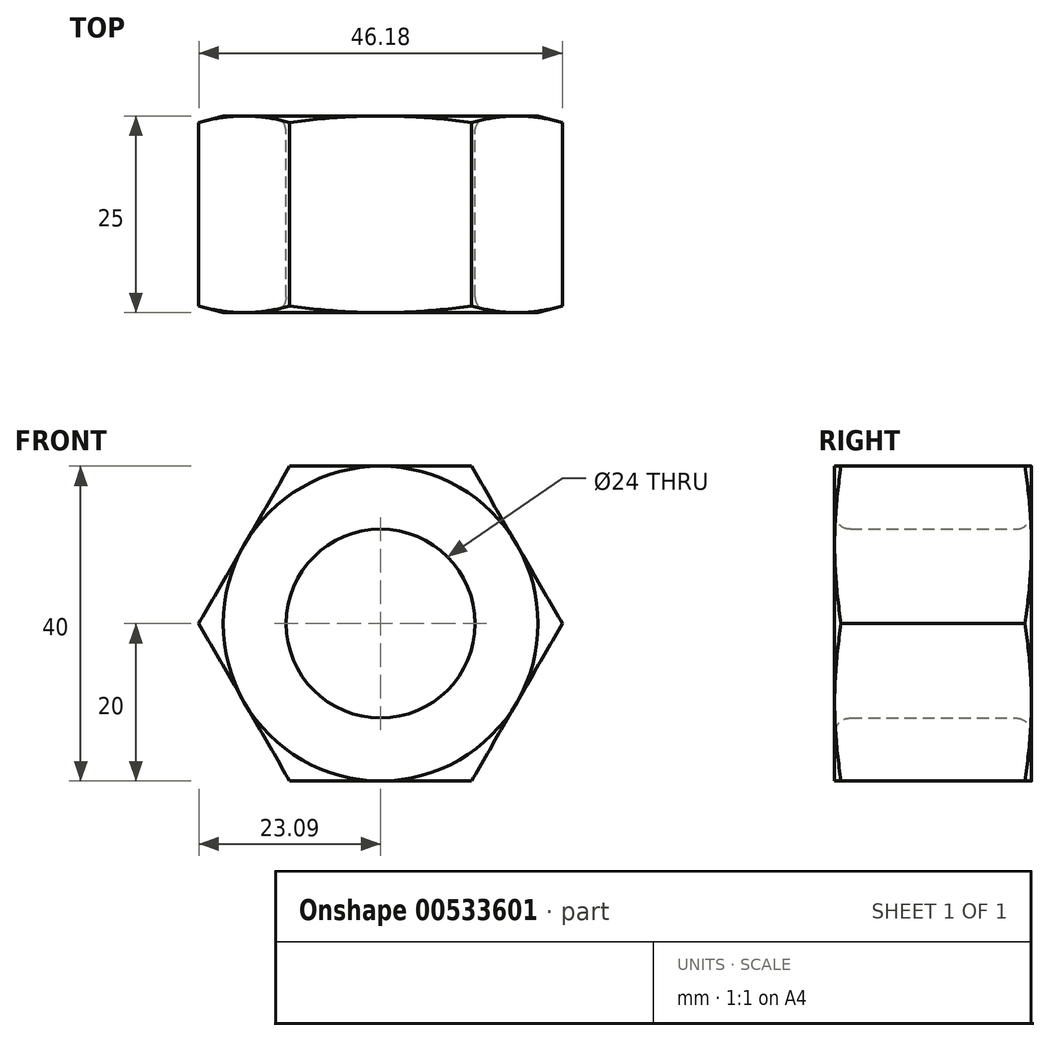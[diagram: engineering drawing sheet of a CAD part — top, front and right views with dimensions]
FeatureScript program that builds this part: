
annotation { "Feature Type Name" : "Feature", "Feature Type Description" : "" }
export const myFeature = defineFeature(function(context is Context, id is Id, definition is map)
    precondition{}
    {
        {
            var Q0;
            Q0=qCreatedBy(makeId("Front.planeOp"),FACE);
            var sketch = newSketch(context, id + "F0", { "sketchPlane" : qUnion([Q0])});
            skCircle(sketch, "E0.cCircle", {"center": v(0, 0) * mm, "radius": 20 * mm, "construction": true});
            skLineSegment(sketch, "E0.0", {"start": v(-11.55, 20) * mm, "end": v(11.55, 20) * mm});
            skLineSegment(sketch, "E0.1", {"start": v(11.55, 20) * mm, "end": v(23.1, 0) * mm});
            skLineSegment(sketch, "E0.2", {"start": v(23.1, 0) * mm, "end": v(11.55, -20) * mm});
            skLineSegment(sketch, "E0.3", {"start": v(11.55, -20) * mm, "end": v(-11.55, -20) * mm});
            skLineSegment(sketch, "E0.4", {"start": v(-11.55, -20) * mm, "end": v(-23.1, 0) * mm});
            skLineSegment(sketch, "E0.5", {"start": v(-23.1, 0) * mm, "end": v(-11.55, 20) * mm});
            skPoint(sketch, "E0.0.midPoint", {"position": v(0, 20) * mm});
            skCircle(sketch, "E1", {"center": v(0, 0) * mm, "radius": 12 * mm});
            skSolve(sketch);
        }
        {
            var Q0;
            Q0=qSketchRegion(id+"F0",true);
            extrude(context, id + "F1", {"entities" : qUnion([Q0]), "depth" : 25 * mm});
        }
        {
            var Q0;
            Q0=qCreatedBy(makeId("Right.planeOp"),FACE);
            var sketch = newSketch(context, id + "F2", { "sketchPlane" : qUnion([Q0])});
            skLineSegment(sketch, "E2", {"start": v(-25, 20) * mm, "end": v(-18.84, 42.98) * mm});
            skLineSegment(sketch, "E3", {"start": v(-18.84, 42.98) * mm, "end": v(-6.16, 42.98) * mm});
            skLineSegment(sketch, "E4", {"start": v(-6.16, 42.98) * mm, "end": v(0, 20) * mm});
            skLineSegment(sketch, "E5", {"start": v(0, 20) * mm, "end": v(0, 56.94) * mm});
            skLineSegment(sketch, "E6", {"start": v(0, 56.94) * mm, "end": v(-25, 56.94) * mm});
            skLineSegment(sketch, "E7", {"start": v(-25, 56.94) * mm, "end": v(-25, 20) * mm});
            skLineSegment(sketch, "E8", {"start": v(-54.18, 0) * mm, "end": v(47.95, 0) * mm});
            skSolve(sketch);
        }
        {
            var Q0;
            Q0=makeQuery(id+"F2.imprint","IMPRINT",FACE,{"disambiguationData":[TD([[makeQuery(id+"F2.imprint","IMPRINT",EDGE,{"derivedFrom":sQuery(id+"F2.wireOp",EDGE,"E2")}),1.0]])]});
            var Q1;
            Q1=sQuery(id+"F2.wireOp",EDGE,"E8");
            revolve(context, id + "F3", {"operationType" : NewBodyOperationType.REMOVE, "entities" : qUnion([Q0]), "axis" : qUnion([Q1]), "revolveType" : RevolveType.FULL, "oppositeDirection" : true});
        }
        {
            var Q0;
            Q0=makeQuery(id+"F1.opExtrude","CAP_EDGE",EDGE,{"disambiguationData":[OSD([sQuery(id+"F0.wireOp",EDGE,"E1")])],"isStart":false});
            var Q1;
            Q1=makeQuery(id+"F1.opExtrude","CAP_EDGE",EDGE,{"disambiguationData":[OSD([sQuery(id+"F0.wireOp",EDGE,"E1")])],"isStart":true});
            fillet(context, id + "F4", {"entities" : qUnion([Q0, Q1]), "radius" : 2 * mm, "tangentPropagation" : true, "allowEdgeOverflow" : false});
        }
    });
